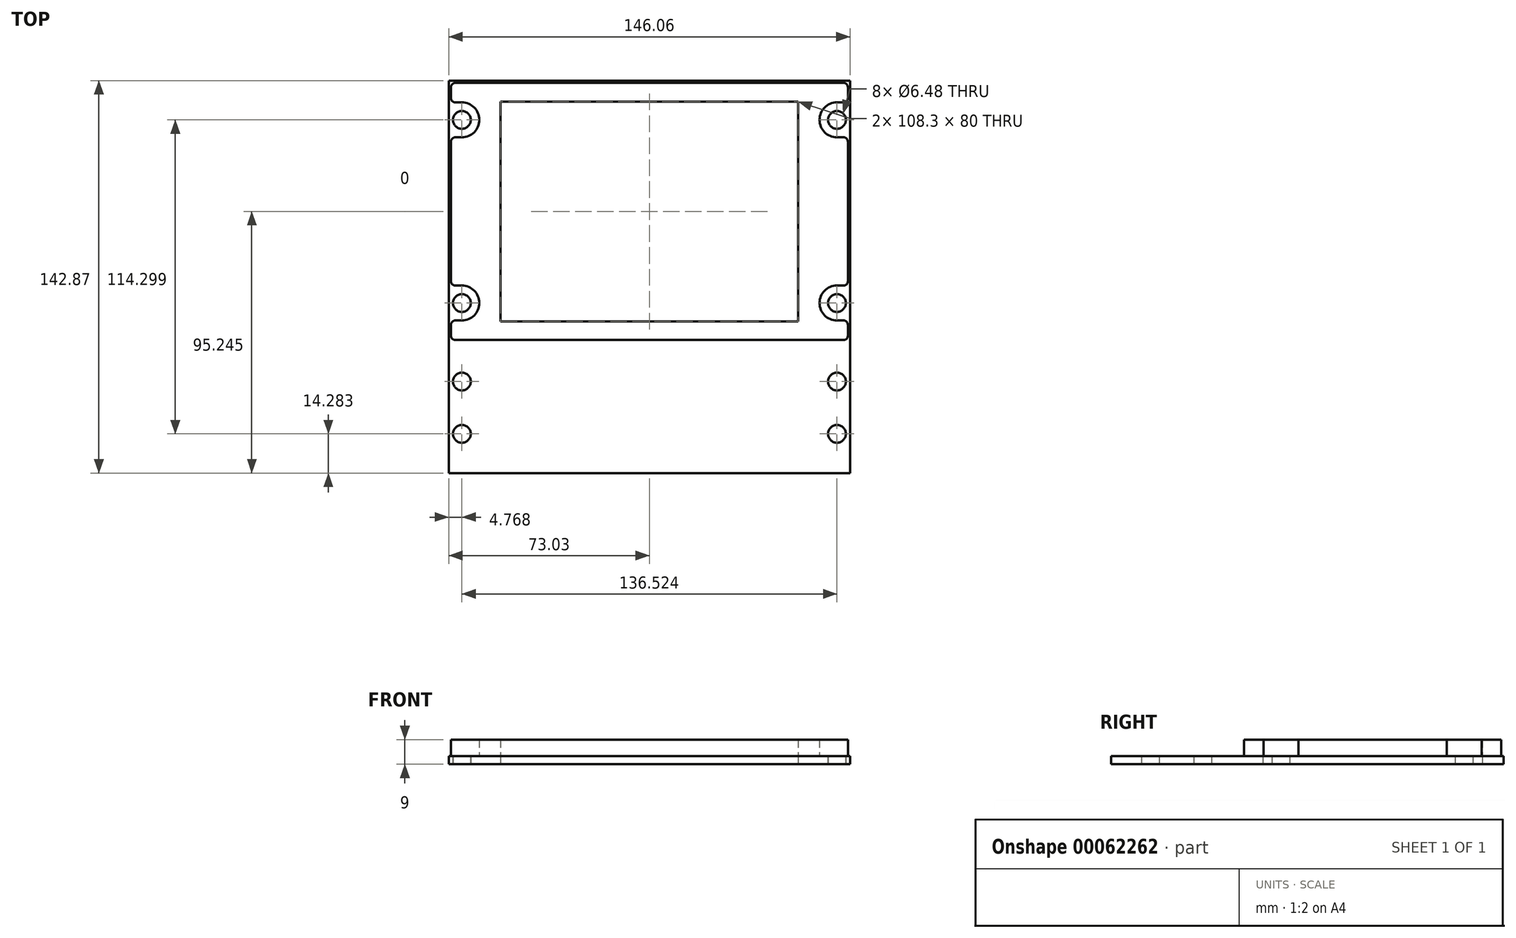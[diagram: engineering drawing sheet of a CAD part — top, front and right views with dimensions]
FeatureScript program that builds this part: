
annotation { "Feature Type Name" : "Feature", "Feature Type Description" : "" }
export const myFeature = defineFeature(function(context is Context, id is Id, definition is map)
    precondition{}
    {
        {
            var Q0;
            Q0=qCreatedBy(makeId("Top.planeOp"),FACE);
            var sketch = newSketch(context, id + "F0", { "sketchPlane" : qUnion([Q0])});
            skLineSegment(sketch, "E0.bottom", {"start": v(-73.03, 57.15) * mm, "end": v(73.03, 57.15) * mm});
            skLineSegment(sketch, "E0.top", {"start": v(-73.03, -38.1) * mm, "end": v(73.03, -38.1) * mm});
            skLineSegment(sketch, "E0.left", {"start": v(-73.03, 57.15) * mm, "end": v(-73.02, -38.1) * mm});
            skLineSegment(sketch, "E0.right", {"start": v(73.03, 57.15) * mm, "end": v(73.03, -38.1) * mm});
            skCircle(sketch, "E1", {"center": v(-68.26, 42.86) * mm, "radius": 3.24 * mm});
            skLineSegment(sketch, "E2", {"start": v(-73.03, 9.52) * mm, "end": v(-67.9, 9.52) * mm});
            skLineSegment(sketch, "E3.MirrorCS", {"start": v(73.03, 57.15) * mm, "end": v(73.02, -38.1) * mm});
            skCircle(sketch, "E4.MirrorC", {"center": v(68.26, 42.86) * mm, "radius": 3.24 * mm});
            skLineSegment(sketch, "E5.bottom", {"start": v(-72.23, 56.35) * mm, "end": v(72.23, 56.35) * mm});
            skLineSegment(sketch, "E5.top", {"start": v(-72.23, -37.3) * mm, "end": v(72.23, -37.3) * mm});
            skLineSegment(sketch, "E5.left", {"start": v(-72.22, 56.35) * mm, "end": v(-72.22, 49.21) * mm});
            skLineSegment(sketch, "E5.right", {"start": v(72.22, 56.35) * mm, "end": v(72.22, 49.21) * mm});
            skPoint(sketch, "E5.middle", {"position": v(0, 9.52) * mm});
            skPoint(sketch, "E5.middle.positionSnap0", {"position": v(0, 57.15) * mm});
            skPoint(sketch, "E5.centerSnap0", {"position": v(0, 57.15) * mm});
            skLineSegment(sketch, "E6.trimOffspring", {"start": v(-72.22, 36.51) * mm, "end": v(-72.22, -17.46) * mm});
            skCircle(sketch, "E7.MirrorC", {"center": v(-68.26, -23.81) * mm, "radius": 3.24 * mm});
            skLineSegment(sketch, "E8.trimOffspring", {"start": v(-72.22, -30.16) * mm, "end": v(-72.22, -37.3) * mm});
            skLineSegment(sketch, "E9", {"start": v(0, 59.28) * mm, "end": v(0, 57.15) * mm});
            skLineSegment(sketch, "E10.trimOffspring", {"start": v(72.22, 36.51) * mm, "end": v(72.22, -17.46) * mm});
            skLineSegment(sketch, "E11.trimOffspring", {"start": v(72.22, -30.16) * mm, "end": v(72.22, -37.3) * mm});
            skCircle(sketch, "E12.MirrorC", {"center": v(68.26, -23.81) * mm, "radius": 3.24 * mm});
            skLineSegment(sketch, "E13", {"start": v(-68.26, 49.21) * mm, "end": v(-72.22, 49.21) * mm});
            skLineSegment(sketch, "E14", {"start": v(-68.26, 36.51) * mm, "end": v(-72.22, 36.51) * mm});
            skArc(sketch, "E15.trimOffspring", {"start": v(-68.26, 36.51) * mm, "mid": v(-61.91, 42.86) * mm, "end": v(-68.26, 49.21) * mm});
            skLineSegment(sketch, "E16.MirrorCS", {"start": v(68.26, 49.21) * mm, "end": v(72.22, 49.21) * mm});
            skArc(sketch, "E17.MirrorCS", {"start": v(68.26, 36.51) * mm, "mid": v(61.91, 42.86) * mm, "end": v(68.26, 49.21) * mm});
            skLineSegment(sketch, "E18.MirrorCS", {"start": v(68.26, 36.51) * mm, "end": v(72.22, 36.51) * mm});
            skLineSegment(sketch, "E19.MirrorCS", {"start": v(-68.26, -30.16) * mm, "end": v(-72.22, -30.16) * mm});
            skArc(sketch, "E20.MirrorCS", {"start": v(-68.26, -17.46) * mm, "mid": v(-61.91, -23.81) * mm, "end": v(-68.26, -30.16) * mm});
            skLineSegment(sketch, "E21.MirrorCS", {"start": v(-68.26, -17.46) * mm, "end": v(-72.22, -17.46) * mm});
            skLineSegment(sketch, "E22.MirrorCS", {"start": v(68.26, -30.16) * mm, "end": v(72.23, -30.16) * mm});
            skArc(sketch, "E23.MirrorCS", {"start": v(68.26, -17.46) * mm, "mid": v(61.91, -23.81) * mm, "end": v(68.26, -30.16) * mm});
            skLineSegment(sketch, "E24.MirrorCS", {"start": v(68.26, -17.46) * mm, "end": v(72.23, -17.46) * mm});
            skSolve(sketch);
        }
        {
            var Q0;
            {var subQ3=sQuery(id+"F0.wireOp",EDGE,"E0.bottom");Q0=makeQuery(id+"F0.imprint","IMPRINT",FACE,{"disambiguationData":[TD([[makeQuery(id+"F0.imprint","IMPRINT",EDGE,{"derivedFrom":subQ3}),-1.0]])]});}
            var Q1;
            Q1=makeQuery(id+"F0.imprint","IMPRINT",FACE,{"disambiguationData":[TD([[makeQuery(id+"F0.imprint","IMPRINT",EDGE,{"derivedFrom":sQuery(id+"F0.wireOp",EDGE,"0KsHYRzl-QeBp-Sicu-B30s-vmT9e8yUwkHf")}),-1.0]])]});
            var Q2;
            {var subQ5=sQuery(id+"F0.wireOp",EDGE,"E0.top");Q2=makeQuery(id+"F0.imprint","IMPRINT",FACE,{"disambiguationData":[TD([[makeQuery(id+"F0.imprint","IMPRINT",EDGE,{"derivedFrom":subQ5}),1.0]])]});}
            var Q3;
            Q3=makeQuery(id+"F0.imprint","IMPRINT",FACE,{"disambiguationData":[TD([[makeQuery(id+"F0.imprint","IMPRINT",EDGE,{"derivedFrom":sQuery(id+"F0.wireOp",EDGE,"E5.bottom")}),-1.0]])]});
            extrude(context, id + "F1", {"entities" : qUnion([Q0, Q1, Q2, Q3]), "oppositeDirection" : true, "depth" : 3 * mm, "offsetDistance" : 25 * mm});
        }
        {
            var Q0;
            Q0=makeQuery(id+"F0.imprint","IMPRINT",FACE,{"disambiguationData":[TD([[makeQuery(id+"F0.imprint","IMPRINT",EDGE,{"derivedFrom":sQuery(id+"F0.wireOp",EDGE,"E5.bottom")}),-1.0]])]});
            extrude(context, id + "F2", {"entities" : qUnion([Q0]), "depth" : 6 * mm, "offsetDistance" : 25 * mm});
        }
        {
            var Q0;
            Q0=makeQuery(id+"F2.opExtrude","SWEPT_EDGE",EDGE,{"disambiguationData":[OSD([sQuery(id+"F0.wireOp",EDGE,"E5.bottom"),sQuery(id+"F0.wireOp",EDGE,"E5.left")])]});
            var Q1;
            Q1=makeQuery(id+"F2.opExtrude","SWEPT_EDGE",EDGE,{"disambiguationData":[OSD([sQuery(id+"F0.wireOp",EDGE,"E5.left"),sQuery(id+"F0.wireOp",EDGE,"KYFBzgIQ-4Zqs-6R5z-qhiH-rvfPci5RRXDs")])]});
            var Q2;
            Q2=makeQuery(id+"F2.opExtrude","SWEPT_EDGE",EDGE,{"disambiguationData":[OSD([sQuery(id+"F0.wireOp",EDGE,"y0Ednotj-fgLE-47Of-3iWq-vnumbfe9Me7E"),sQuery(id+"F0.wireOp",EDGE,"E6.trimOffspring")])]});
            var Q3;
            Q3=makeQuery(id+"F2.opExtrude","SWEPT_EDGE",EDGE,{"disambiguationData":[OSD([sQuery(id+"F0.wireOp",EDGE,"E6.trimOffspring"),sQuery(id+"F0.wireOp",EDGE,"553364b0-0c50-41da-a4d1-f82c899684470.MirrorCS")])]});
            var Q4;
            Q4=makeQuery(id+"F2.opExtrude","SWEPT_EDGE",EDGE,{"disambiguationData":[OSD([sQuery(id+"F0.wireOp",EDGE,"2d0b2af7-1972-4472-80e1-425fef26b84a0.MirrorCS"),sQuery(id+"F0.wireOp",EDGE,"E8.trimOffspring")])]});
            var Q5;
            Q5=makeQuery(id+"F2.opExtrude","SWEPT_EDGE",EDGE,{"disambiguationData":[OSD([sQuery(id+"F0.wireOp",EDGE,"E5.top"),sQuery(id+"F0.wireOp",EDGE,"E8.trimOffspring")])]});
            var Q6;
            Q6=makeQuery(id+"F2.opExtrude","SWEPT_EDGE",EDGE,{"disambiguationData":[OSD([sQuery(id+"F0.wireOp",EDGE,"E5.top"),sQuery(id+"F0.wireOp",EDGE,"E11.trimOffspring")])]});
            var Q7;
            Q7=makeQuery(id+"F2.opExtrude","SWEPT_EDGE",EDGE,{"disambiguationData":[OSD([sQuery(id+"F0.wireOp",EDGE,"6b0da2aa-3882-46fa-a501-ba939454f24d0.MirrorCS"),sQuery(id+"F0.wireOp",EDGE,"E11.trimOffspring")])]});
            var Q8;
            Q8=makeQuery(id+"F2.opExtrude","SWEPT_EDGE",EDGE,{"disambiguationData":[OSD([sQuery(id+"F0.wireOp",EDGE,"23beaa88-9077-45f1-bc4f-ba4309250fa40.MirrorCS"),sQuery(id+"F0.wireOp",EDGE,"E10.trimOffspring")])]});
            var Q9;
            Q9=makeQuery(id+"F2.opExtrude","SWEPT_EDGE",EDGE,{"disambiguationData":[OSD([sQuery(id+"F0.wireOp",EDGE,"E5.right"),sQuery(id+"F0.wireOp",EDGE,"76e7f314-1e51-4c87-a9a9-bf629407e17e0.MirrorCS")])]});
            var Q10;
            Q10=makeQuery(id+"F2.opExtrude","SWEPT_EDGE",EDGE,{"disambiguationData":[OSD([sQuery(id+"F0.wireOp",EDGE,"E5.bottom"),sQuery(id+"F0.wireOp",EDGE,"E5.right")])]});
            var Q11;
            Q11=makeQuery(id+"F2.opExtrude","SWEPT_EDGE",EDGE,{"disambiguationData":[OSD([sQuery(id+"F0.wireOp",EDGE,"fdf2bb90-056c-49c9-a4f4-28e15fb56c020.MirrorCS"),sQuery(id+"F0.wireOp",EDGE,"E10.trimOffspring")])]});
            fillet(context, id + "F3", {"entities" : qUnion([Q0, Q1, Q2, Q3, Q4, Q5, Q6, Q7, Q8, Q9, Q10, Q11]), "radius" : 1.59 * mm, "tangentPropagation" : true, "allowEdgeOverflow" : false});
        }
        {
            var Q0;
            Q0=makeQuery(id+"F2.opExtrude","CAP_FACE",FACE,{"disambiguationData":[OSD([sQuery(id+"F0.wireOp",EDGE,"0KsHYRzl-QeBp-Sicu-B30s-vmT9e8yUwkHf"),sQuery(id+"F0.wireOp",EDGE,"E5.bottom"),sQuery(id+"F0.wireOp",EDGE,"E5.top"),sQuery(id+"F0.wireOp",EDGE,"E5.left"),sQuery(id+"F0.wireOp",EDGE,"E5.right"),sQuery(id+"F0.wireOp",EDGE,"KYFBzgIQ-4Zqs-6R5z-qhiH-rvfPci5RRXDs"),sQuery(id+"F0.wireOp",EDGE,"y0Ednotj-fgLE-47Of-3iWq-vnumbfe9Me7E"),sQuery(id+"F0.wireOp",EDGE,"E6.trimOffspring"),sQuery(id+"F0.wireOp",EDGE,"2a2d7b29-b02f-4e17-9193-bcc7f10cbe761.MirrorCS"),sQuery(id+"F0.wireOp",EDGE,"2d0b2af7-1972-4472-80e1-425fef26b84a0.MirrorCS"),sQuery(id+"F0.wireOp",EDGE,"553364b0-0c50-41da-a4d1-f82c899684470.MirrorCS"),sQuery(id+"F0.wireOp",EDGE,"E8.trimOffspring"),sQuery(id+"F0.wireOp",EDGE,"76e7f314-1e51-4c87-a9a9-bf629407e17e0.MirrorCS"),sQuery(id+"F0.wireOp",EDGE,"802900b7-2ba9-4d70-825f-09b2bce8e5960.MirrorCS"),sQuery(id+"F0.wireOp",EDGE,"fdf2bb90-056c-49c9-a4f4-28e15fb56c020.MirrorCS"),sQuery(id+"F0.wireOp",EDGE,"23beaa88-9077-45f1-bc4f-ba4309250fa40.MirrorCS"),sQuery(id+"F0.wireOp",EDGE,"49d2e7f7-8f5b-4fc1-bffe-4eb2e1ab077b0.MirrorCS"),sQuery(id+"F0.wireOp",EDGE,"6b0da2aa-3882-46fa-a501-ba939454f24d0.MirrorCS"),sQuery(id+"F0.wireOp",EDGE,"E10.trimOffspring"),sQuery(id+"F0.wireOp",EDGE,"E11.trimOffspring")])],"isStart":false});
            var sketch = newSketch(context, id + "F4", { "sketchPlane" : qUnion([Q0])});
            skLineSegment(sketch, "E25", {"start": v(0, 56.35) * mm, "end": v(0, 54.26) * mm});
            skLineSegment(sketch, "E26.bottom", {"start": v(-2, 49.52) * mm, "end": v(-26, 49.52) * mm});
            skLineSegment(sketch, "E26.top", {"start": v(-2, 41.52) * mm, "end": v(-26, 41.52) * mm});
            skLineSegment(sketch, "E26.left", {"start": v(-2, 49.52) * mm, "end": v(-2, 41.52) * mm});
            skLineSegment(sketch, "E26.right", {"start": v(-26, 49.52) * mm, "end": v(-26, 41.52) * mm});
            skLineSegment(sketch, "E27.bottom", {"start": v(-30, 49.52) * mm, "end": v(-54.15, 49.52) * mm});
            skLineSegment(sketch, "E27.top", {"start": v(-30, 41.52) * mm, "end": v(-54.15, 41.52) * mm});
            skLineSegment(sketch, "E27.left", {"start": v(-30, 49.52) * mm, "end": v(-30, 41.52) * mm});
            skLineSegment(sketch, "E27.right", {"start": v(-54.15, 49.52) * mm, "end": v(-54.15, 41.52) * mm});
            skLineSegment(sketch, "E28.MirrorCS", {"start": v(30, 41.52) * mm, "end": v(54.15, 41.52) * mm});
            skLineSegment(sketch, "E29.MirrorCS", {"start": v(2, 41.52) * mm, "end": v(26, 41.52) * mm});
            skLineSegment(sketch, "E30.MirrorCS", {"start": v(30, 49.52) * mm, "end": v(54.15, 49.52) * mm});
            skLineSegment(sketch, "E31.MirrorCS", {"start": v(2, 49.52) * mm, "end": v(2, 41.52) * mm});
            skLineSegment(sketch, "E32.MirrorCS", {"start": v(30, 49.52) * mm, "end": v(30, 41.52) * mm});
            skLineSegment(sketch, "E33.MirrorCS", {"start": v(2, 49.52) * mm, "end": v(26, 49.52) * mm});
            skLineSegment(sketch, "E34.MirrorCS", {"start": v(26, 49.52) * mm, "end": v(26, 41.52) * mm});
            skLineSegment(sketch, "E35.MirrorCS", {"start": v(54.15, 49.52) * mm, "end": v(54.15, 41.52) * mm});
            skLineSegment(sketch, "E36.0.1.0", {"start": v(-2, 37.52) * mm, "end": v(-26, 37.52) * mm});
            skLineSegment(sketch, "E36.0.1.1", {"start": v(-30, 29.52) * mm, "end": v(-54.15, 29.52) * mm});
            skLineSegment(sketch, "E36.0.1.2", {"start": v(26, 37.52) * mm, "end": v(26, 29.52) * mm});
            skLineSegment(sketch, "E36.0.1.3", {"start": v(30, 37.52) * mm, "end": v(54.15, 37.52) * mm});
            skLineSegment(sketch, "E36.0.1.4", {"start": v(-26, 37.52) * mm, "end": v(-26, 29.52) * mm});
            skLineSegment(sketch, "E36.0.1.5", {"start": v(30, 29.52) * mm, "end": v(54.15, 29.52) * mm});
            skLineSegment(sketch, "E36.0.1.6", {"start": v(2, 37.52) * mm, "end": v(2, 29.52) * mm});
            skLineSegment(sketch, "E36.0.1.7", {"start": v(30, 37.52) * mm, "end": v(30, 29.52) * mm});
            skLineSegment(sketch, "E36.0.1.8", {"start": v(-54.15, 37.52) * mm, "end": v(-54.15, 29.52) * mm});
            skLineSegment(sketch, "E36.0.1.9", {"start": v(54.15, 37.53) * mm, "end": v(54.15, 29.52) * mm});
            skLineSegment(sketch, "E36.0.1.10", {"start": v(-2, 37.52) * mm, "end": v(-2, 29.52) * mm});
            skLineSegment(sketch, "E36.0.1.11", {"start": v(2, 29.52) * mm, "end": v(26, 29.52) * mm});
            skLineSegment(sketch, "E36.0.1.12", {"start": v(2, 37.52) * mm, "end": v(26, 37.52) * mm});
            skLineSegment(sketch, "E36.0.1.13", {"start": v(-30, 37.52) * mm, "end": v(-30, 29.52) * mm});
            skLineSegment(sketch, "E36.0.1.14", {"start": v(-30, 37.52) * mm, "end": v(-54.15, 37.52) * mm});
            skLineSegment(sketch, "E36.0.1.15", {"start": v(-2, 29.52) * mm, "end": v(-26, 29.52) * mm});
            skLineSegment(sketch, "E36.0.2.0", {"start": v(-2, 25.52) * mm, "end": v(-26, 25.52) * mm});
            skLineSegment(sketch, "E36.0.2.1", {"start": v(-30, 17.52) * mm, "end": v(-54.15, 17.52) * mm});
            skLineSegment(sketch, "E36.0.2.2", {"start": v(26, 25.52) * mm, "end": v(26, 17.52) * mm});
            skLineSegment(sketch, "E36.0.2.3", {"start": v(30, 25.52) * mm, "end": v(54.15, 25.52) * mm});
            skLineSegment(sketch, "E36.0.2.4", {"start": v(-26, 25.52) * mm, "end": v(-26, 17.52) * mm});
            skLineSegment(sketch, "E36.0.2.5", {"start": v(30, 17.52) * mm, "end": v(54.15, 17.52) * mm});
            skLineSegment(sketch, "E36.0.2.6", {"start": v(2, 25.52) * mm, "end": v(2, 17.52) * mm});
            skLineSegment(sketch, "E36.0.2.7", {"start": v(30, 25.52) * mm, "end": v(30, 17.52) * mm});
            skLineSegment(sketch, "E36.0.2.8", {"start": v(-54.15, 25.52) * mm, "end": v(-54.15, 17.52) * mm});
            skLineSegment(sketch, "E36.0.2.9", {"start": v(54.15, 25.53) * mm, "end": v(54.15, 17.52) * mm});
            skLineSegment(sketch, "E36.0.2.10", {"start": v(-2, 25.52) * mm, "end": v(-2, 17.52) * mm});
            skLineSegment(sketch, "E36.0.2.11", {"start": v(2, 17.52) * mm, "end": v(26, 17.52) * mm});
            skLineSegment(sketch, "E36.0.2.12", {"start": v(2, 25.52) * mm, "end": v(26, 25.52) * mm});
            skLineSegment(sketch, "E36.0.2.13", {"start": v(-30, 25.52) * mm, "end": v(-30, 17.52) * mm});
            skLineSegment(sketch, "E36.0.2.14", {"start": v(-30, 25.52) * mm, "end": v(-54.15, 25.52) * mm});
            skLineSegment(sketch, "E36.0.2.15", {"start": v(-2, 17.52) * mm, "end": v(-26, 17.52) * mm});
            skLineSegment(sketch, "E36.0.3.0", {"start": v(-2, 13.52) * mm, "end": v(-26, 13.52) * mm});
            skLineSegment(sketch, "E36.0.3.1", {"start": v(-30, 5.52) * mm, "end": v(-54.15, 5.52) * mm});
            skLineSegment(sketch, "E36.0.3.2", {"start": v(26, 13.53) * mm, "end": v(26, 5.53) * mm});
            skLineSegment(sketch, "E36.0.3.3", {"start": v(30, 13.52) * mm, "end": v(54.15, 13.52) * mm});
            skLineSegment(sketch, "E36.0.3.4", {"start": v(-26, 13.52) * mm, "end": v(-26, 5.52) * mm});
            skLineSegment(sketch, "E36.0.3.5", {"start": v(30, 5.52) * mm, "end": v(54.15, 5.52) * mm});
            skLineSegment(sketch, "E36.0.3.6", {"start": v(2, 13.52) * mm, "end": v(2, 5.52) * mm});
            skLineSegment(sketch, "E36.0.3.7", {"start": v(30, 13.53) * mm, "end": v(30, 5.53) * mm});
            skLineSegment(sketch, "E36.0.3.8", {"start": v(-54.15, 13.52) * mm, "end": v(-54.15, 5.52) * mm});
            skLineSegment(sketch, "E36.0.3.9", {"start": v(54.15, 13.53) * mm, "end": v(54.15, 5.52) * mm});
            skLineSegment(sketch, "E36.0.3.10", {"start": v(-2, 13.52) * mm, "end": v(-2, 5.52) * mm});
            skLineSegment(sketch, "E36.0.3.11", {"start": v(2, 5.52) * mm, "end": v(26, 5.52) * mm});
            skLineSegment(sketch, "E36.0.3.12", {"start": v(2, 13.52) * mm, "end": v(26, 13.52) * mm});
            skLineSegment(sketch, "E36.0.3.13", {"start": v(-30, 13.52) * mm, "end": v(-30, 5.52) * mm});
            skLineSegment(sketch, "E36.0.3.14", {"start": v(-30, 13.52) * mm, "end": v(-54.15, 13.52) * mm});
            skLineSegment(sketch, "E36.0.3.15", {"start": v(-2, 5.52) * mm, "end": v(-26, 5.52) * mm});
            skLineSegment(sketch, "E36.0.4.0", {"start": v(-2, 1.52) * mm, "end": v(-26, 1.52) * mm});
            skLineSegment(sketch, "E36.0.4.1", {"start": v(-30, -6.48) * mm, "end": v(-54.15, -6.48) * mm});
            skLineSegment(sketch, "E36.0.4.2", {"start": v(26, 1.53) * mm, "end": v(26, -6.47) * mm});
            skLineSegment(sketch, "E36.0.4.3", {"start": v(30, 1.52) * mm, "end": v(54.15, 1.53) * mm});
            skLineSegment(sketch, "E36.0.4.4", {"start": v(-26, 1.52) * mm, "end": v(-26, -6.48) * mm});
            skLineSegment(sketch, "E36.0.4.5", {"start": v(30, -6.48) * mm, "end": v(54.15, -6.47) * mm});
            skLineSegment(sketch, "E36.0.4.6", {"start": v(2, 1.52) * mm, "end": v(2, -6.48) * mm});
            skLineSegment(sketch, "E36.0.4.7", {"start": v(30, 1.53) * mm, "end": v(30, -6.47) * mm});
            skLineSegment(sketch, "E36.0.4.8", {"start": v(-54.15, 1.52) * mm, "end": v(-54.15, -6.48) * mm});
            skLineSegment(sketch, "E36.0.4.9", {"start": v(54.15, 1.53) * mm, "end": v(54.15, -6.48) * mm});
            skLineSegment(sketch, "E36.0.4.10", {"start": v(-2, 1.52) * mm, "end": v(-2, -6.48) * mm});
            skLineSegment(sketch, "E36.0.4.11", {"start": v(2, -6.48) * mm, "end": v(26, -6.47) * mm});
            skLineSegment(sketch, "E36.0.4.12", {"start": v(2, 1.52) * mm, "end": v(26, 1.53) * mm});
            skLineSegment(sketch, "E36.0.4.13", {"start": v(-30, 1.52) * mm, "end": v(-30, -6.48) * mm});
            skLineSegment(sketch, "E36.0.4.14", {"start": v(-30, 1.52) * mm, "end": v(-54.15, 1.52) * mm});
            skLineSegment(sketch, "E36.0.4.15", {"start": v(-2, -6.48) * mm, "end": v(-26, -6.48) * mm});
            skLineSegment(sketch, "E36.0.5.0", {"start": v(-2, -10.47) * mm, "end": v(-26, -10.47) * mm});
            skLineSegment(sketch, "E36.0.5.1", {"start": v(-30, -18.47) * mm, "end": v(-54.15, -18.47) * mm});
            skLineSegment(sketch, "E36.0.5.2", {"start": v(26, -10.47) * mm, "end": v(26, -18.47) * mm});
            skLineSegment(sketch, "E36.0.5.3", {"start": v(30, -10.47) * mm, "end": v(54.15, -10.47) * mm});
            skLineSegment(sketch, "E36.0.5.4", {"start": v(-26, -10.47) * mm, "end": v(-26, -18.47) * mm});
            skLineSegment(sketch, "E36.0.5.5", {"start": v(30, -18.47) * mm, "end": v(54.15, -18.47) * mm});
            skLineSegment(sketch, "E36.0.5.6", {"start": v(2, -10.47) * mm, "end": v(2, -18.47) * mm});
            skLineSegment(sketch, "E36.0.5.7", {"start": v(30, -10.47) * mm, "end": v(30, -18.47) * mm});
            skLineSegment(sketch, "E36.0.5.8", {"start": v(-54.15, -10.47) * mm, "end": v(-54.15, -18.47) * mm});
            skLineSegment(sketch, "E36.0.5.9", {"start": v(54.15, -10.47) * mm, "end": v(54.15, -18.47) * mm});
            skLineSegment(sketch, "E36.0.5.10", {"start": v(-2, -10.47) * mm, "end": v(-2, -18.47) * mm});
            skLineSegment(sketch, "E36.0.5.11", {"start": v(2, -18.47) * mm, "end": v(26, -18.47) * mm});
            skLineSegment(sketch, "E36.0.5.12", {"start": v(2, -10.47) * mm, "end": v(26, -10.47) * mm});
            skLineSegment(sketch, "E36.0.5.13", {"start": v(-30, -10.47) * mm, "end": v(-30, -18.47) * mm});
            skLineSegment(sketch, "E36.0.5.14", {"start": v(-30, -10.47) * mm, "end": v(-54.15, -10.47) * mm});
            skLineSegment(sketch, "E36.0.5.15", {"start": v(-2, -18.47) * mm, "end": v(-26, -18.47) * mm});
            skLineSegment(sketch, "E36.0.6.0", {"start": v(-2, -22.47) * mm, "end": v(-26, -22.47) * mm});
            skLineSegment(sketch, "E36.0.6.1", {"start": v(-30, -30.47) * mm, "end": v(-54.15, -30.47) * mm});
            skLineSegment(sketch, "E36.0.6.2", {"start": v(26, -22.47) * mm, "end": v(26, -30.47) * mm});
            skLineSegment(sketch, "E36.0.6.3", {"start": v(30, -22.47) * mm, "end": v(54.15, -22.47) * mm});
            skLineSegment(sketch, "E36.0.6.4", {"start": v(-26, -22.47) * mm, "end": v(-26, -30.47) * mm});
            skLineSegment(sketch, "E36.0.6.5", {"start": v(30, -30.47) * mm, "end": v(54.15, -30.47) * mm});
            skLineSegment(sketch, "E36.0.6.6", {"start": v(2, -22.47) * mm, "end": v(2, -30.47) * mm});
            skLineSegment(sketch, "E36.0.6.7", {"start": v(30, -22.47) * mm, "end": v(30, -30.47) * mm});
            skLineSegment(sketch, "E36.0.6.8", {"start": v(-54.15, -22.47) * mm, "end": v(-54.15, -30.47) * mm});
            skLineSegment(sketch, "E36.0.6.9", {"start": v(54.15, -22.47) * mm, "end": v(54.15, -30.47) * mm});
            skLineSegment(sketch, "E36.0.6.10", {"start": v(-2, -22.47) * mm, "end": v(-2, -30.47) * mm});
            skLineSegment(sketch, "E36.0.6.11", {"start": v(2, -30.47) * mm, "end": v(26, -30.47) * mm});
            skLineSegment(sketch, "E36.0.6.12", {"start": v(2, -22.47) * mm, "end": v(26, -22.47) * mm});
            skLineSegment(sketch, "E36.0.6.13", {"start": v(-30, -22.47) * mm, "end": v(-30, -30.47) * mm});
            skLineSegment(sketch, "E36.0.6.14", {"start": v(-30, -22.47) * mm, "end": v(-54.15, -22.47) * mm});
            skLineSegment(sketch, "E36.0.6.15", {"start": v(-2, -30.47) * mm, "end": v(-26, -30.47) * mm});
            skLineSegment(sketch, "E36.direction1", {"start": v(-54.15, 41.52) * mm, "end": v(-29.15, 41.52) * mm, "construction": true});
            skLineSegment(sketch, "E36.direction2", {"start": v(-54.15, 41.52) * mm, "end": v(-54.15, 29.52) * mm, "construction": true});
            skLineSegment(sketch, "E37", {"start": v(-2, 9.52) * mm, "end": v(-6.78, 9.52) * mm});
            skSolve(sketch);
        }
        {
            var Q0;
            Q0 = qSketchRegion(id + "F4", true);
            extrude(context, id + "F5", {"entities" : qUnion([Q0]), "operationType" : NewBodyOperationType.REMOVE, "oppositeDirection" : true, "depth" : 25 * mm, "offsetDistance" : 25 * mm});
        }
        {
            var Q0;
            Q0=makeQuery(id+"F5.boolean.opBoolean","COPY",EDGE,{"derivedFrom":makeQuery(id+"F5.opExtrude","SWEPT_EDGE",EDGE,{"disambiguationData":[OSD([sQuery(id+"F4.wireOp",EDGE,"E27.bottom"),sQuery(id+"F4.wireOp",EDGE,"E27.right")])]})});
            var Q1;
            Q1=makeQuery(id+"F5.boolean.opBoolean","COPY",EDGE,{"derivedFrom":makeQuery(id+"F5.opExtrude","SWEPT_EDGE",EDGE,{"disambiguationData":[OSD([sQuery(id+"F4.wireOp",EDGE,"E27.top"),sQuery(id+"F4.wireOp",EDGE,"E27.right")])]})});
            var Q2;
            Q2=makeQuery(id+"F5.boolean.opBoolean","COPY",EDGE,{"derivedFrom":makeQuery(id+"F5.opExtrude","SWEPT_EDGE",EDGE,{"disambiguationData":[OSD([sQuery(id+"F4.wireOp",EDGE,"E27.top"),sQuery(id+"F4.wireOp",EDGE,"E27.left")])]})});
            var Q3;
            Q3=makeQuery(id+"F5.boolean.opBoolean","COPY",EDGE,{"derivedFrom":makeQuery(id+"F5.opExtrude","SWEPT_EDGE",EDGE,{"disambiguationData":[OSD([sQuery(id+"F4.wireOp",EDGE,"E27.bottom"),sQuery(id+"F4.wireOp",EDGE,"E27.left")])]})});
            var Q4;
            Q4=makeQuery(id+"F5.boolean.opBoolean","COPY",EDGE,{"derivedFrom":makeQuery(id+"F5.opExtrude","SWEPT_EDGE",EDGE,{"disambiguationData":[OSD([sQuery(id+"F4.wireOp",EDGE,"E36.0.1.13"),sQuery(id+"F4.wireOp",EDGE,"E36.0.1.14")])]})});
            var Q5;
            Q5=makeQuery(id+"F5.boolean.opBoolean","COPY",EDGE,{"derivedFrom":makeQuery(id+"F5.opExtrude","SWEPT_EDGE",EDGE,{"disambiguationData":[OSD([sQuery(id+"F4.wireOp",EDGE,"E36.0.2.13"),sQuery(id+"F4.wireOp",EDGE,"E36.0.2.14")])]})});
            var Q6;
            Q6=makeQuery(id+"F5.boolean.opBoolean","COPY",EDGE,{"derivedFrom":makeQuery(id+"F5.opExtrude","SWEPT_EDGE",EDGE,{"disambiguationData":[OSD([sQuery(id+"F4.wireOp",EDGE,"E36.0.3.13"),sQuery(id+"F4.wireOp",EDGE,"E36.0.3.14")])]})});
            var Q7;
            Q7=makeQuery(id+"F5.boolean.opBoolean","COPY",EDGE,{"derivedFrom":makeQuery(id+"F5.opExtrude","SWEPT_EDGE",EDGE,{"disambiguationData":[OSD([sQuery(id+"F4.wireOp",EDGE,"E36.0.4.13"),sQuery(id+"F4.wireOp",EDGE,"E36.0.4.14")])]})});
            var Q8;
            Q8=makeQuery(id+"F5.boolean.opBoolean","COPY",EDGE,{"derivedFrom":makeQuery(id+"F5.opExtrude","SWEPT_EDGE",EDGE,{"disambiguationData":[OSD([sQuery(id+"F4.wireOp",EDGE,"E36.0.5.13"),sQuery(id+"F4.wireOp",EDGE,"E36.0.5.14")])]})});
            var Q9;
            Q9=makeQuery(id+"F5.boolean.opBoolean","COPY",EDGE,{"derivedFrom":makeQuery(id+"F5.opExtrude","SWEPT_EDGE",EDGE,{"disambiguationData":[OSD([sQuery(id+"F4.wireOp",EDGE,"E36.0.6.13"),sQuery(id+"F4.wireOp",EDGE,"E36.0.6.14")])]})});
            var Q10;
            Q10=makeQuery(id+"F5.boolean.opBoolean","COPY",EDGE,{"derivedFrom":makeQuery(id+"F5.opExtrude","SWEPT_EDGE",EDGE,{"disambiguationData":[OSD([sQuery(id+"F4.wireOp",EDGE,"E36.0.6.0"),sQuery(id+"F4.wireOp",EDGE,"E36.0.6.10")])]})});
            var Q11;
            Q11=makeQuery(id+"F5.boolean.opBoolean","COPY",EDGE,{"derivedFrom":makeQuery(id+"F5.opExtrude","SWEPT_EDGE",EDGE,{"disambiguationData":[OSD([sQuery(id+"F4.wireOp",EDGE,"E36.0.5.0"),sQuery(id+"F4.wireOp",EDGE,"E36.0.5.10")])]})});
            var Q12;
            Q12=makeQuery(id+"F5.boolean.opBoolean","COPY",EDGE,{"derivedFrom":makeQuery(id+"F5.opExtrude","SWEPT_EDGE",EDGE,{"disambiguationData":[OSD([sQuery(id+"F4.wireOp",EDGE,"E36.0.4.0"),sQuery(id+"F4.wireOp",EDGE,"E36.0.4.10")])]})});
            var Q13;
            Q13=makeQuery(id+"F5.boolean.opBoolean","COPY",EDGE,{"derivedFrom":makeQuery(id+"F5.opExtrude","SWEPT_EDGE",EDGE,{"disambiguationData":[OSD([sQuery(id+"F4.wireOp",EDGE,"E36.0.3.0"),sQuery(id+"F4.wireOp",EDGE,"E36.0.3.10")])]})});
            var Q14;
            Q14=makeQuery(id+"F5.boolean.opBoolean","COPY",EDGE,{"derivedFrom":makeQuery(id+"F5.opExtrude","SWEPT_EDGE",EDGE,{"disambiguationData":[OSD([sQuery(id+"F4.wireOp",EDGE,"E36.0.2.0"),sQuery(id+"F4.wireOp",EDGE,"E36.0.2.10")])]})});
            var Q15;
            Q15=makeQuery(id+"F5.boolean.opBoolean","COPY",EDGE,{"derivedFrom":makeQuery(id+"F5.opExtrude","SWEPT_EDGE",EDGE,{"disambiguationData":[OSD([sQuery(id+"F4.wireOp",EDGE,"E36.0.1.0"),sQuery(id+"F4.wireOp",EDGE,"E36.0.1.10")])]})});
            var Q16;
            Q16=makeQuery(id+"F5.boolean.opBoolean","COPY",EDGE,{"derivedFrom":makeQuery(id+"F5.opExtrude","SWEPT_EDGE",EDGE,{"disambiguationData":[OSD([sQuery(id+"F4.wireOp",EDGE,"E26.bottom"),sQuery(id+"F4.wireOp",EDGE,"E26.left")])]})});
            var Q17;
            Q17=makeQuery(id+"F5.boolean.opBoolean","COPY",EDGE,{"derivedFrom":makeQuery(id+"F5.opExtrude","SWEPT_EDGE",EDGE,{"disambiguationData":[OSD([sQuery(id+"F4.wireOp",EDGE,"E33.MirrorCS"),sQuery(id+"F4.wireOp",EDGE,"E34.MirrorCS")])]})});
            var Q18;
            Q18=makeQuery(id+"F5.boolean.opBoolean","COPY",EDGE,{"derivedFrom":makeQuery(id+"F5.opExtrude","SWEPT_EDGE",EDGE,{"disambiguationData":[OSD([sQuery(id+"F4.wireOp",EDGE,"E36.0.1.2"),sQuery(id+"F4.wireOp",EDGE,"E36.0.1.12")])]})});
            var Q19;
            Q19=makeQuery(id+"F5.boolean.opBoolean","COPY",EDGE,{"derivedFrom":makeQuery(id+"F5.opExtrude","SWEPT_EDGE",EDGE,{"disambiguationData":[OSD([sQuery(id+"F4.wireOp",EDGE,"E36.0.2.2"),sQuery(id+"F4.wireOp",EDGE,"E36.0.2.12")])]})});
            var Q20;
            Q20=makeQuery(id+"F5.boolean.opBoolean","COPY",EDGE,{"derivedFrom":makeQuery(id+"F5.opExtrude","SWEPT_EDGE",EDGE,{"disambiguationData":[OSD([sQuery(id+"F4.wireOp",EDGE,"E36.0.3.2"),sQuery(id+"F4.wireOp",EDGE,"E36.0.3.12")])]})});
            var Q21;
            Q21=makeQuery(id+"F5.boolean.opBoolean","COPY",EDGE,{"derivedFrom":makeQuery(id+"F5.opExtrude","SWEPT_EDGE",EDGE,{"disambiguationData":[OSD([sQuery(id+"F4.wireOp",EDGE,"E36.0.4.2"),sQuery(id+"F4.wireOp",EDGE,"E36.0.4.12")])]})});
            var Q22;
            Q22=makeQuery(id+"F5.boolean.opBoolean","COPY",EDGE,{"derivedFrom":makeQuery(id+"F5.opExtrude","SWEPT_EDGE",EDGE,{"disambiguationData":[OSD([sQuery(id+"F4.wireOp",EDGE,"E36.0.5.2"),sQuery(id+"F4.wireOp",EDGE,"E36.0.5.12")])]})});
            var Q23;
            Q23=makeQuery(id+"F5.boolean.opBoolean","COPY",EDGE,{"derivedFrom":makeQuery(id+"F5.opExtrude","SWEPT_EDGE",EDGE,{"disambiguationData":[OSD([sQuery(id+"F4.wireOp",EDGE,"E36.0.6.2"),sQuery(id+"F4.wireOp",EDGE,"E36.0.6.12")])]})});
            var Q24;
            Q24=makeQuery(id+"F5.boolean.opBoolean","COPY",EDGE,{"derivedFrom":makeQuery(id+"F5.opExtrude","SWEPT_EDGE",EDGE,{"disambiguationData":[OSD([sQuery(id+"F4.wireOp",EDGE,"E36.0.6.3"),sQuery(id+"F4.wireOp",EDGE,"E36.0.6.9")])]})});
            var Q25;
            Q25=makeQuery(id+"F5.boolean.opBoolean","COPY",EDGE,{"derivedFrom":makeQuery(id+"F5.opExtrude","SWEPT_EDGE",EDGE,{"disambiguationData":[OSD([sQuery(id+"F4.wireOp",EDGE,"E36.0.5.3"),sQuery(id+"F4.wireOp",EDGE,"E36.0.5.9")])]})});
            var Q26;
            Q26=makeQuery(id+"F5.boolean.opBoolean","COPY",EDGE,{"derivedFrom":makeQuery(id+"F5.opExtrude","SWEPT_EDGE",EDGE,{"disambiguationData":[OSD([sQuery(id+"F4.wireOp",EDGE,"E36.0.4.3"),sQuery(id+"F4.wireOp",EDGE,"E36.0.4.9")])]})});
            var Q27;
            Q27=makeQuery(id+"F5.boolean.opBoolean","COPY",EDGE,{"derivedFrom":makeQuery(id+"F5.opExtrude","SWEPT_EDGE",EDGE,{"disambiguationData":[OSD([sQuery(id+"F4.wireOp",EDGE,"E36.0.3.3"),sQuery(id+"F4.wireOp",EDGE,"E36.0.3.9")])]})});
            var Q28;
            Q28=makeQuery(id+"F5.boolean.opBoolean","COPY",EDGE,{"derivedFrom":makeQuery(id+"F5.opExtrude","SWEPT_EDGE",EDGE,{"disambiguationData":[OSD([sQuery(id+"F4.wireOp",EDGE,"E36.0.2.3"),sQuery(id+"F4.wireOp",EDGE,"E36.0.2.9")])]})});
            var Q29;
            Q29=makeQuery(id+"F5.boolean.opBoolean","COPY",EDGE,{"derivedFrom":makeQuery(id+"F5.opExtrude","SWEPT_EDGE",EDGE,{"disambiguationData":[OSD([sQuery(id+"F4.wireOp",EDGE,"E36.0.1.3"),sQuery(id+"F4.wireOp",EDGE,"E36.0.1.9")])]})});
            var Q30;
            Q30=makeQuery(id+"F5.boolean.opBoolean","COPY",EDGE,{"derivedFrom":makeQuery(id+"F5.opExtrude","SWEPT_EDGE",EDGE,{"disambiguationData":[OSD([sQuery(id+"F4.wireOp",EDGE,"E30.MirrorCS"),sQuery(id+"F4.wireOp",EDGE,"E35.MirrorCS")])]})});
            var Q31;
            Q31=makeQuery(id+"F5.boolean.opBoolean","COPY",EDGE,{"derivedFrom":makeQuery(id+"F5.opExtrude","SWEPT_EDGE",EDGE,{"disambiguationData":[OSD([sQuery(id+"F4.wireOp",EDGE,"E26.top"),sQuery(id+"F4.wireOp",EDGE,"E26.left")])]})});
            var Q32;
            Q32=makeQuery(id+"F5.boolean.opBoolean","COPY",EDGE,{"derivedFrom":makeQuery(id+"F5.opExtrude","SWEPT_EDGE",EDGE,{"disambiguationData":[OSD([sQuery(id+"F4.wireOp",EDGE,"E29.MirrorCS"),sQuery(id+"F4.wireOp",EDGE,"E34.MirrorCS")])]})});
            var Q33;
            Q33=makeQuery(id+"F5.boolean.opBoolean","COPY",EDGE,{"derivedFrom":makeQuery(id+"F5.opExtrude","SWEPT_EDGE",EDGE,{"disambiguationData":[OSD([sQuery(id+"F4.wireOp",EDGE,"E28.MirrorCS"),sQuery(id+"F4.wireOp",EDGE,"E35.MirrorCS")])]})});
            var Q34;
            Q34=makeQuery(id+"F5.boolean.opBoolean","COPY",EDGE,{"derivedFrom":makeQuery(id+"F5.opExtrude","SWEPT_EDGE",EDGE,{"disambiguationData":[OSD([sQuery(id+"F4.wireOp",EDGE,"E36.0.1.1"),sQuery(id+"F4.wireOp",EDGE,"E36.0.1.13")])]})});
            var Q35;
            Q35=makeQuery(id+"F5.boolean.opBoolean","COPY",EDGE,{"derivedFrom":makeQuery(id+"F5.opExtrude","SWEPT_EDGE",EDGE,{"disambiguationData":[OSD([sQuery(id+"F4.wireOp",EDGE,"E36.0.1.10"),sQuery(id+"F4.wireOp",EDGE,"E36.0.1.15")])]})});
            var Q36;
            Q36=makeQuery(id+"F5.boolean.opBoolean","COPY",EDGE,{"derivedFrom":makeQuery(id+"F5.opExtrude","SWEPT_EDGE",EDGE,{"disambiguationData":[OSD([sQuery(id+"F4.wireOp",EDGE,"E36.0.1.2"),sQuery(id+"F4.wireOp",EDGE,"E36.0.1.11")])]})});
            var Q37;
            Q37=makeQuery(id+"F5.boolean.opBoolean","COPY",EDGE,{"derivedFrom":makeQuery(id+"F5.opExtrude","SWEPT_EDGE",EDGE,{"disambiguationData":[OSD([sQuery(id+"F4.wireOp",EDGE,"E36.0.1.5"),sQuery(id+"F4.wireOp",EDGE,"E36.0.1.9")])]})});
            var Q38;
            Q38=makeQuery(id+"F5.boolean.opBoolean","COPY",EDGE,{"derivedFrom":makeQuery(id+"F5.opExtrude","SWEPT_EDGE",EDGE,{"disambiguationData":[OSD([sQuery(id+"F4.wireOp",EDGE,"E36.0.2.5"),sQuery(id+"F4.wireOp",EDGE,"E36.0.2.9")])]})});
            var Q39;
            Q39=makeQuery(id+"F5.boolean.opBoolean","COPY",EDGE,{"derivedFrom":makeQuery(id+"F5.opExtrude","SWEPT_EDGE",EDGE,{"disambiguationData":[OSD([sQuery(id+"F4.wireOp",EDGE,"E36.0.2.2"),sQuery(id+"F4.wireOp",EDGE,"E36.0.2.11")])]})});
            var Q40;
            Q40=makeQuery(id+"F5.boolean.opBoolean","COPY",EDGE,{"derivedFrom":makeQuery(id+"F5.opExtrude","SWEPT_EDGE",EDGE,{"disambiguationData":[OSD([sQuery(id+"F4.wireOp",EDGE,"E36.0.2.10"),sQuery(id+"F4.wireOp",EDGE,"E36.0.2.15")])]})});
            var Q41;
            Q41=makeQuery(id+"F5.boolean.opBoolean","COPY",EDGE,{"derivedFrom":makeQuery(id+"F5.opExtrude","SWEPT_EDGE",EDGE,{"disambiguationData":[OSD([sQuery(id+"F4.wireOp",EDGE,"E36.0.2.1"),sQuery(id+"F4.wireOp",EDGE,"E36.0.2.13")])]})});
            var Q42;
            Q42=makeQuery(id+"F5.boolean.opBoolean","COPY",EDGE,{"derivedFrom":makeQuery(id+"F5.opExtrude","SWEPT_EDGE",EDGE,{"disambiguationData":[OSD([sQuery(id+"F4.wireOp",EDGE,"E36.0.3.1"),sQuery(id+"F4.wireOp",EDGE,"E36.0.3.13")])]})});
            var Q43;
            Q43=makeQuery(id+"F5.boolean.opBoolean","COPY",EDGE,{"derivedFrom":makeQuery(id+"F5.opExtrude","SWEPT_EDGE",EDGE,{"disambiguationData":[OSD([sQuery(id+"F4.wireOp",EDGE,"E36.0.4.1"),sQuery(id+"F4.wireOp",EDGE,"E36.0.4.13")])]})});
            var Q44;
            Q44=makeQuery(id+"F5.boolean.opBoolean","COPY",EDGE,{"derivedFrom":makeQuery(id+"F5.opExtrude","SWEPT_EDGE",EDGE,{"disambiguationData":[OSD([sQuery(id+"F4.wireOp",EDGE,"E36.0.5.1"),sQuery(id+"F4.wireOp",EDGE,"E36.0.5.13")])]})});
            var Q45;
            Q45=makeQuery(id+"F5.boolean.opBoolean","COPY",EDGE,{"derivedFrom":makeQuery(id+"F5.opExtrude","SWEPT_EDGE",EDGE,{"disambiguationData":[OSD([sQuery(id+"F4.wireOp",EDGE,"E36.0.6.1"),sQuery(id+"F4.wireOp",EDGE,"E36.0.6.13")])]})});
            var Q46;
            Q46=makeQuery(id+"F5.boolean.opBoolean","COPY",EDGE,{"derivedFrom":makeQuery(id+"F5.opExtrude","SWEPT_EDGE",EDGE,{"disambiguationData":[OSD([sQuery(id+"F4.wireOp",EDGE,"E36.0.6.10"),sQuery(id+"F4.wireOp",EDGE,"E36.0.6.15")])]})});
            var Q47;
            Q47=makeQuery(id+"F5.boolean.opBoolean","COPY",EDGE,{"derivedFrom":makeQuery(id+"F5.opExtrude","SWEPT_EDGE",EDGE,{"disambiguationData":[OSD([sQuery(id+"F4.wireOp",EDGE,"E36.0.5.10"),sQuery(id+"F4.wireOp",EDGE,"E36.0.5.15")])]})});
            var Q48;
            Q48=makeQuery(id+"F5.boolean.opBoolean","COPY",EDGE,{"derivedFrom":makeQuery(id+"F5.opExtrude","SWEPT_EDGE",EDGE,{"disambiguationData":[OSD([sQuery(id+"F4.wireOp",EDGE,"E36.0.4.10"),sQuery(id+"F4.wireOp",EDGE,"E36.0.4.15")])]})});
            var Q49;
            Q49=makeQuery(id+"F5.boolean.opBoolean","COPY",EDGE,{"derivedFrom":makeQuery(id+"F5.opExtrude","SWEPT_EDGE",EDGE,{"disambiguationData":[OSD([sQuery(id+"F4.wireOp",EDGE,"E36.0.3.10"),sQuery(id+"F4.wireOp",EDGE,"E36.0.3.15")])]})});
            var Q50;
            Q50=makeQuery(id+"F5.boolean.opBoolean","COPY",EDGE,{"derivedFrom":makeQuery(id+"F5.opExtrude","SWEPT_EDGE",EDGE,{"disambiguationData":[OSD([sQuery(id+"F4.wireOp",EDGE,"E36.0.3.2"),sQuery(id+"F4.wireOp",EDGE,"E36.0.3.11")])]})});
            var Q51;
            Q51=makeQuery(id+"F5.boolean.opBoolean","COPY",EDGE,{"derivedFrom":makeQuery(id+"F5.opExtrude","SWEPT_EDGE",EDGE,{"disambiguationData":[OSD([sQuery(id+"F4.wireOp",EDGE,"E36.0.3.5"),sQuery(id+"F4.wireOp",EDGE,"E36.0.3.9")])]})});
            var Q52;
            Q52=makeQuery(id+"F5.boolean.opBoolean","COPY",EDGE,{"derivedFrom":makeQuery(id+"F5.opExtrude","SWEPT_EDGE",EDGE,{"disambiguationData":[OSD([sQuery(id+"F4.wireOp",EDGE,"E36.0.4.2"),sQuery(id+"F4.wireOp",EDGE,"E36.0.4.11")])]})});
            var Q53;
            Q53=makeQuery(id+"F5.boolean.opBoolean","COPY",EDGE,{"derivedFrom":makeQuery(id+"F5.opExtrude","SWEPT_EDGE",EDGE,{"disambiguationData":[OSD([sQuery(id+"F4.wireOp",EDGE,"E36.0.4.5"),sQuery(id+"F4.wireOp",EDGE,"E36.0.4.9")])]})});
            var Q54;
            Q54=makeQuery(id+"F5.boolean.opBoolean","COPY",EDGE,{"derivedFrom":makeQuery(id+"F5.opExtrude","SWEPT_EDGE",EDGE,{"disambiguationData":[OSD([sQuery(id+"F4.wireOp",EDGE,"E36.0.5.5"),sQuery(id+"F4.wireOp",EDGE,"E36.0.5.9")])]})});
            var Q55;
            Q55=makeQuery(id+"F5.boolean.opBoolean","COPY",EDGE,{"derivedFrom":makeQuery(id+"F5.opExtrude","SWEPT_EDGE",EDGE,{"disambiguationData":[OSD([sQuery(id+"F4.wireOp",EDGE,"E36.0.5.2"),sQuery(id+"F4.wireOp",EDGE,"E36.0.5.11")])]})});
            var Q56;
            Q56=makeQuery(id+"F5.boolean.opBoolean","COPY",EDGE,{"derivedFrom":makeQuery(id+"F5.opExtrude","SWEPT_EDGE",EDGE,{"disambiguationData":[OSD([sQuery(id+"F4.wireOp",EDGE,"E36.0.6.2"),sQuery(id+"F4.wireOp",EDGE,"E36.0.6.11")])]})});
            var Q57;
            Q57=makeQuery(id+"F5.boolean.opBoolean","COPY",EDGE,{"derivedFrom":makeQuery(id+"F5.opExtrude","SWEPT_EDGE",EDGE,{"disambiguationData":[OSD([sQuery(id+"F4.wireOp",EDGE,"E36.0.6.5"),sQuery(id+"F4.wireOp",EDGE,"E36.0.6.9")])]})});
            var Q58;
            Q58=makeQuery(id+"F5.boolean.opBoolean","COPY",EDGE,{"derivedFrom":makeQuery(id+"F5.opExtrude","SWEPT_EDGE",EDGE,{"disambiguationData":[OSD([sQuery(id+"F4.wireOp",EDGE,"E26.top"),sQuery(id+"F4.wireOp",EDGE,"E26.right")])]})});
            var Q59;
            Q59=makeQuery(id+"F5.boolean.opBoolean","COPY",EDGE,{"derivedFrom":makeQuery(id+"F5.opExtrude","SWEPT_EDGE",EDGE,{"disambiguationData":[OSD([sQuery(id+"F4.wireOp",EDGE,"E29.MirrorCS"),sQuery(id+"F4.wireOp",EDGE,"E31.MirrorCS")])]})});
            var Q60;
            Q60=makeQuery(id+"F5.boolean.opBoolean","COPY",EDGE,{"derivedFrom":makeQuery(id+"F5.opExtrude","SWEPT_EDGE",EDGE,{"disambiguationData":[OSD([sQuery(id+"F4.wireOp",EDGE,"E28.MirrorCS"),sQuery(id+"F4.wireOp",EDGE,"E32.MirrorCS")])]})});
            var Q61;
            Q61=makeQuery(id+"F5.boolean.opBoolean","COPY",EDGE,{"derivedFrom":makeQuery(id+"F5.opExtrude","SWEPT_EDGE",EDGE,{"disambiguationData":[OSD([sQuery(id+"F4.wireOp",EDGE,"E36.0.1.5"),sQuery(id+"F4.wireOp",EDGE,"E36.0.1.7")])]})});
            var Q62;
            Q62=makeQuery(id+"F5.boolean.opBoolean","COPY",EDGE,{"derivedFrom":makeQuery(id+"F5.opExtrude","SWEPT_EDGE",EDGE,{"disambiguationData":[OSD([sQuery(id+"F4.wireOp",EDGE,"E36.0.1.6"),sQuery(id+"F4.wireOp",EDGE,"E36.0.1.11")])]})});
            var Q63;
            Q63=makeQuery(id+"F5.boolean.opBoolean","COPY",EDGE,{"derivedFrom":makeQuery(id+"F5.opExtrude","SWEPT_EDGE",EDGE,{"disambiguationData":[OSD([sQuery(id+"F4.wireOp",EDGE,"E36.0.1.4"),sQuery(id+"F4.wireOp",EDGE,"E36.0.1.15")])]})});
            var Q64;
            Q64=makeQuery(id+"F5.boolean.opBoolean","COPY",EDGE,{"derivedFrom":makeQuery(id+"F5.opExtrude","SWEPT_EDGE",EDGE,{"disambiguationData":[OSD([sQuery(id+"F4.wireOp",EDGE,"E36.0.1.1"),sQuery(id+"F4.wireOp",EDGE,"E36.0.1.8")])]})});
            var Q65;
            Q65=makeQuery(id+"F5.boolean.opBoolean","COPY",EDGE,{"derivedFrom":makeQuery(id+"F5.opExtrude","SWEPT_EDGE",EDGE,{"disambiguationData":[OSD([sQuery(id+"F4.wireOp",EDGE,"E36.0.2.1"),sQuery(id+"F4.wireOp",EDGE,"E36.0.2.8")])]})});
            var Q66;
            Q66=makeQuery(id+"F5.boolean.opBoolean","COPY",EDGE,{"derivedFrom":makeQuery(id+"F5.opExtrude","SWEPT_EDGE",EDGE,{"disambiguationData":[OSD([sQuery(id+"F4.wireOp",EDGE,"E36.0.2.4"),sQuery(id+"F4.wireOp",EDGE,"E36.0.2.15")])]})});
            var Q67;
            Q67=makeQuery(id+"F5.boolean.opBoolean","COPY",EDGE,{"derivedFrom":makeQuery(id+"F5.opExtrude","SWEPT_EDGE",EDGE,{"disambiguationData":[OSD([sQuery(id+"F4.wireOp",EDGE,"E36.0.2.6"),sQuery(id+"F4.wireOp",EDGE,"E36.0.2.11")])]})});
            var Q68;
            Q68=makeQuery(id+"F5.boolean.opBoolean","COPY",EDGE,{"derivedFrom":makeQuery(id+"F5.opExtrude","SWEPT_EDGE",EDGE,{"disambiguationData":[OSD([sQuery(id+"F4.wireOp",EDGE,"E36.0.2.5"),sQuery(id+"F4.wireOp",EDGE,"E36.0.2.7")])]})});
            var Q69;
            Q69=makeQuery(id+"F5.boolean.opBoolean","COPY",EDGE,{"derivedFrom":makeQuery(id+"F5.opExtrude","SWEPT_EDGE",EDGE,{"disambiguationData":[OSD([sQuery(id+"F4.wireOp",EDGE,"E36.0.3.5"),sQuery(id+"F4.wireOp",EDGE,"E36.0.3.7")])]})});
            var Q70;
            Q70=makeQuery(id+"F5.boolean.opBoolean","COPY",EDGE,{"derivedFrom":makeQuery(id+"F5.opExtrude","SWEPT_EDGE",EDGE,{"disambiguationData":[OSD([sQuery(id+"F4.wireOp",EDGE,"E36.0.3.6"),sQuery(id+"F4.wireOp",EDGE,"E36.0.3.11")])]})});
            var Q71;
            Q71=makeQuery(id+"F5.boolean.opBoolean","COPY",EDGE,{"derivedFrom":makeQuery(id+"F5.opExtrude","SWEPT_EDGE",EDGE,{"disambiguationData":[OSD([sQuery(id+"F4.wireOp",EDGE,"E36.0.3.4"),sQuery(id+"F4.wireOp",EDGE,"E36.0.3.15")])]})});
            var Q72;
            Q72=makeQuery(id+"F5.boolean.opBoolean","COPY",EDGE,{"derivedFrom":makeQuery(id+"F5.opExtrude","SWEPT_EDGE",EDGE,{"disambiguationData":[OSD([sQuery(id+"F4.wireOp",EDGE,"E36.0.3.1"),sQuery(id+"F4.wireOp",EDGE,"E36.0.3.8")])]})});
            var Q73;
            Q73=makeQuery(id+"F5.boolean.opBoolean","COPY",EDGE,{"derivedFrom":makeQuery(id+"F5.opExtrude","SWEPT_EDGE",EDGE,{"disambiguationData":[OSD([sQuery(id+"F4.wireOp",EDGE,"E36.0.4.1"),sQuery(id+"F4.wireOp",EDGE,"E36.0.4.8")])]})});
            var Q74;
            Q74=makeQuery(id+"F5.boolean.opBoolean","COPY",EDGE,{"derivedFrom":makeQuery(id+"F5.opExtrude","SWEPT_EDGE",EDGE,{"disambiguationData":[OSD([sQuery(id+"F4.wireOp",EDGE,"E36.0.4.4"),sQuery(id+"F4.wireOp",EDGE,"E36.0.4.15")])]})});
            var Q75;
            Q75=makeQuery(id+"F5.boolean.opBoolean","COPY",EDGE,{"derivedFrom":makeQuery(id+"F5.opExtrude","SWEPT_EDGE",EDGE,{"disambiguationData":[OSD([sQuery(id+"F4.wireOp",EDGE,"E36.0.4.6"),sQuery(id+"F4.wireOp",EDGE,"E36.0.4.11")])]})});
            var Q76;
            Q76=makeQuery(id+"F5.boolean.opBoolean","COPY",EDGE,{"derivedFrom":makeQuery(id+"F5.opExtrude","SWEPT_EDGE",EDGE,{"disambiguationData":[OSD([sQuery(id+"F4.wireOp",EDGE,"E36.0.4.5"),sQuery(id+"F4.wireOp",EDGE,"E36.0.4.7")])]})});
            var Q77;
            Q77=makeQuery(id+"F5.boolean.opBoolean","COPY",EDGE,{"derivedFrom":makeQuery(id+"F5.opExtrude","SWEPT_EDGE",EDGE,{"disambiguationData":[OSD([sQuery(id+"F4.wireOp",EDGE,"E36.0.5.5"),sQuery(id+"F4.wireOp",EDGE,"E36.0.5.7")])]})});
            var Q78;
            Q78=makeQuery(id+"F5.boolean.opBoolean","COPY",EDGE,{"derivedFrom":makeQuery(id+"F5.opExtrude","SWEPT_EDGE",EDGE,{"disambiguationData":[OSD([sQuery(id+"F4.wireOp",EDGE,"E36.0.5.6"),sQuery(id+"F4.wireOp",EDGE,"E36.0.5.11")])]})});
            var Q79;
            Q79=makeQuery(id+"F5.boolean.opBoolean","COPY",EDGE,{"derivedFrom":makeQuery(id+"F5.opExtrude","SWEPT_EDGE",EDGE,{"disambiguationData":[OSD([sQuery(id+"F4.wireOp",EDGE,"E36.0.5.4"),sQuery(id+"F4.wireOp",EDGE,"E36.0.5.15")])]})});
            var Q80;
            Q80=makeQuery(id+"F5.boolean.opBoolean","COPY",EDGE,{"derivedFrom":makeQuery(id+"F5.opExtrude","SWEPT_EDGE",EDGE,{"disambiguationData":[OSD([sQuery(id+"F4.wireOp",EDGE,"E36.0.5.1"),sQuery(id+"F4.wireOp",EDGE,"E36.0.5.8")])]})});
            var Q81;
            Q81=makeQuery(id+"F5.boolean.opBoolean","COPY",EDGE,{"derivedFrom":makeQuery(id+"F5.opExtrude","SWEPT_EDGE",EDGE,{"disambiguationData":[OSD([sQuery(id+"F4.wireOp",EDGE,"E36.0.6.1"),sQuery(id+"F4.wireOp",EDGE,"E36.0.6.8")])]})});
            var Q82;
            Q82=makeQuery(id+"F5.boolean.opBoolean","COPY",EDGE,{"derivedFrom":makeQuery(id+"F5.opExtrude","SWEPT_EDGE",EDGE,{"disambiguationData":[OSD([sQuery(id+"F4.wireOp",EDGE,"E36.0.6.4"),sQuery(id+"F4.wireOp",EDGE,"E36.0.6.15")])]})});
            var Q83;
            Q83=makeQuery(id+"F5.boolean.opBoolean","COPY",EDGE,{"derivedFrom":makeQuery(id+"F5.opExtrude","SWEPT_EDGE",EDGE,{"disambiguationData":[OSD([sQuery(id+"F4.wireOp",EDGE,"E36.0.6.6"),sQuery(id+"F4.wireOp",EDGE,"E36.0.6.11")])]})});
            var Q84;
            Q84=makeQuery(id+"F5.boolean.opBoolean","COPY",EDGE,{"derivedFrom":makeQuery(id+"F5.opExtrude","SWEPT_EDGE",EDGE,{"disambiguationData":[OSD([sQuery(id+"F4.wireOp",EDGE,"E36.0.6.5"),sQuery(id+"F4.wireOp",EDGE,"E36.0.6.7")])]})});
            var Q85;
            Q85=makeQuery(id+"F5.boolean.opBoolean","COPY",EDGE,{"derivedFrom":makeQuery(id+"F5.opExtrude","SWEPT_EDGE",EDGE,{"disambiguationData":[OSD([sQuery(id+"F4.wireOp",EDGE,"E26.bottom"),sQuery(id+"F4.wireOp",EDGE,"E26.right")])]})});
            var Q86;
            Q86=makeQuery(id+"F5.boolean.opBoolean","COPY",EDGE,{"derivedFrom":makeQuery(id+"F5.opExtrude","SWEPT_EDGE",EDGE,{"disambiguationData":[OSD([sQuery(id+"F4.wireOp",EDGE,"E31.MirrorCS"),sQuery(id+"F4.wireOp",EDGE,"E33.MirrorCS")])]})});
            var Q87;
            Q87=makeQuery(id+"F5.boolean.opBoolean","COPY",EDGE,{"derivedFrom":makeQuery(id+"F5.opExtrude","SWEPT_EDGE",EDGE,{"disambiguationData":[OSD([sQuery(id+"F4.wireOp",EDGE,"E30.MirrorCS"),sQuery(id+"F4.wireOp",EDGE,"E32.MirrorCS")])]})});
            var Q88;
            Q88=makeQuery(id+"F5.boolean.opBoolean","COPY",EDGE,{"derivedFrom":makeQuery(id+"F5.opExtrude","SWEPT_EDGE",EDGE,{"disambiguationData":[OSD([sQuery(id+"F4.wireOp",EDGE,"E36.0.1.8"),sQuery(id+"F4.wireOp",EDGE,"E36.0.1.14")])]})});
            var Q89;
            Q89=makeQuery(id+"F5.boolean.opBoolean","COPY",EDGE,{"derivedFrom":makeQuery(id+"F5.opExtrude","SWEPT_EDGE",EDGE,{"disambiguationData":[OSD([sQuery(id+"F4.wireOp",EDGE,"E36.0.1.0"),sQuery(id+"F4.wireOp",EDGE,"E36.0.1.4")])]})});
            var Q90;
            Q90=makeQuery(id+"F5.boolean.opBoolean","COPY",EDGE,{"derivedFrom":makeQuery(id+"F5.opExtrude","SWEPT_EDGE",EDGE,{"disambiguationData":[OSD([sQuery(id+"F4.wireOp",EDGE,"E36.0.1.6"),sQuery(id+"F4.wireOp",EDGE,"E36.0.1.12")])]})});
            var Q91;
            Q91=makeQuery(id+"F5.boolean.opBoolean","COPY",EDGE,{"derivedFrom":makeQuery(id+"F5.opExtrude","SWEPT_EDGE",EDGE,{"disambiguationData":[OSD([sQuery(id+"F4.wireOp",EDGE,"E36.0.1.3"),sQuery(id+"F4.wireOp",EDGE,"E36.0.1.7")])]})});
            var Q92;
            Q92=makeQuery(id+"F5.boolean.opBoolean","COPY",EDGE,{"derivedFrom":makeQuery(id+"F5.opExtrude","SWEPT_EDGE",EDGE,{"disambiguationData":[OSD([sQuery(id+"F4.wireOp",EDGE,"E36.0.2.8"),sQuery(id+"F4.wireOp",EDGE,"E36.0.2.14")])]})});
            var Q93;
            Q93=makeQuery(id+"F5.boolean.opBoolean","COPY",EDGE,{"derivedFrom":makeQuery(id+"F5.opExtrude","SWEPT_EDGE",EDGE,{"disambiguationData":[OSD([sQuery(id+"F4.wireOp",EDGE,"E36.0.2.0"),sQuery(id+"F4.wireOp",EDGE,"E36.0.2.4")])]})});
            var Q94;
            Q94=makeQuery(id+"F5.boolean.opBoolean","COPY",EDGE,{"derivedFrom":makeQuery(id+"F5.opExtrude","SWEPT_EDGE",EDGE,{"disambiguationData":[OSD([sQuery(id+"F4.wireOp",EDGE,"E36.0.2.6"),sQuery(id+"F4.wireOp",EDGE,"E36.0.2.12")])]})});
            var Q95;
            Q95=makeQuery(id+"F5.boolean.opBoolean","COPY",EDGE,{"derivedFrom":makeQuery(id+"F5.opExtrude","SWEPT_EDGE",EDGE,{"disambiguationData":[OSD([sQuery(id+"F4.wireOp",EDGE,"E36.0.2.3"),sQuery(id+"F4.wireOp",EDGE,"E36.0.2.7")])]})});
            var Q96;
            Q96=makeQuery(id+"F5.boolean.opBoolean","COPY",EDGE,{"derivedFrom":makeQuery(id+"F5.opExtrude","SWEPT_EDGE",EDGE,{"disambiguationData":[OSD([sQuery(id+"F4.wireOp",EDGE,"E36.0.3.8"),sQuery(id+"F4.wireOp",EDGE,"E36.0.3.14")])]})});
            var Q97;
            Q97=makeQuery(id+"F5.boolean.opBoolean","COPY",EDGE,{"derivedFrom":makeQuery(id+"F5.opExtrude","SWEPT_EDGE",EDGE,{"disambiguationData":[OSD([sQuery(id+"F4.wireOp",EDGE,"E36.0.3.0"),sQuery(id+"F4.wireOp",EDGE,"E36.0.3.4")])]})});
            var Q98;
            Q98=makeQuery(id+"F5.boolean.opBoolean","COPY",EDGE,{"derivedFrom":makeQuery(id+"F5.opExtrude","SWEPT_EDGE",EDGE,{"disambiguationData":[OSD([sQuery(id+"F4.wireOp",EDGE,"E36.0.3.6"),sQuery(id+"F4.wireOp",EDGE,"E36.0.3.12")])]})});
            var Q99;
            Q99=makeQuery(id+"F5.boolean.opBoolean","COPY",EDGE,{"derivedFrom":makeQuery(id+"F5.opExtrude","SWEPT_EDGE",EDGE,{"disambiguationData":[OSD([sQuery(id+"F4.wireOp",EDGE,"E36.0.3.3"),sQuery(id+"F4.wireOp",EDGE,"E36.0.3.7")])]})});
            var Q100;
            Q100=makeQuery(id+"F5.boolean.opBoolean","COPY",EDGE,{"derivedFrom":makeQuery(id+"F5.opExtrude","SWEPT_EDGE",EDGE,{"disambiguationData":[OSD([sQuery(id+"F4.wireOp",EDGE,"E36.0.4.8"),sQuery(id+"F4.wireOp",EDGE,"E36.0.4.14")])]})});
            var Q101;
            Q101=makeQuery(id+"F5.boolean.opBoolean","COPY",EDGE,{"derivedFrom":makeQuery(id+"F5.opExtrude","SWEPT_EDGE",EDGE,{"disambiguationData":[OSD([sQuery(id+"F4.wireOp",EDGE,"E36.0.4.0"),sQuery(id+"F4.wireOp",EDGE,"E36.0.4.4")])]})});
            var Q102;
            Q102=makeQuery(id+"F5.boolean.opBoolean","COPY",EDGE,{"derivedFrom":makeQuery(id+"F5.opExtrude","SWEPT_EDGE",EDGE,{"disambiguationData":[OSD([sQuery(id+"F4.wireOp",EDGE,"E36.0.4.6"),sQuery(id+"F4.wireOp",EDGE,"E36.0.4.12")])]})});
            var Q103;
            Q103=makeQuery(id+"F5.boolean.opBoolean","COPY",EDGE,{"derivedFrom":makeQuery(id+"F5.opExtrude","SWEPT_EDGE",EDGE,{"disambiguationData":[OSD([sQuery(id+"F4.wireOp",EDGE,"E36.0.4.3"),sQuery(id+"F4.wireOp",EDGE,"E36.0.4.7")])]})});
            var Q104;
            Q104=makeQuery(id+"F5.boolean.opBoolean","COPY",EDGE,{"derivedFrom":makeQuery(id+"F5.opExtrude","SWEPT_EDGE",EDGE,{"disambiguationData":[OSD([sQuery(id+"F4.wireOp",EDGE,"E36.0.5.8"),sQuery(id+"F4.wireOp",EDGE,"E36.0.5.14")])]})});
            var Q105;
            Q105=makeQuery(id+"F5.boolean.opBoolean","COPY",EDGE,{"derivedFrom":makeQuery(id+"F5.opExtrude","SWEPT_EDGE",EDGE,{"disambiguationData":[OSD([sQuery(id+"F4.wireOp",EDGE,"E36.0.5.0"),sQuery(id+"F4.wireOp",EDGE,"E36.0.5.4")])]})});
            var Q106;
            Q106=makeQuery(id+"F5.boolean.opBoolean","COPY",EDGE,{"derivedFrom":makeQuery(id+"F5.opExtrude","SWEPT_EDGE",EDGE,{"disambiguationData":[OSD([sQuery(id+"F4.wireOp",EDGE,"E36.0.5.6"),sQuery(id+"F4.wireOp",EDGE,"E36.0.5.12")])]})});
            var Q107;
            Q107=makeQuery(id+"F5.boolean.opBoolean","COPY",EDGE,{"derivedFrom":makeQuery(id+"F5.opExtrude","SWEPT_EDGE",EDGE,{"disambiguationData":[OSD([sQuery(id+"F4.wireOp",EDGE,"E36.0.5.3"),sQuery(id+"F4.wireOp",EDGE,"E36.0.5.7")])]})});
            var Q108;
            Q108=makeQuery(id+"F5.boolean.opBoolean","COPY",EDGE,{"derivedFrom":makeQuery(id+"F5.opExtrude","SWEPT_EDGE",EDGE,{"disambiguationData":[OSD([sQuery(id+"F4.wireOp",EDGE,"E36.0.6.8"),sQuery(id+"F4.wireOp",EDGE,"E36.0.6.14")])]})});
            var Q109;
            Q109=makeQuery(id+"F5.boolean.opBoolean","COPY",EDGE,{"derivedFrom":makeQuery(id+"F5.opExtrude","SWEPT_EDGE",EDGE,{"disambiguationData":[OSD([sQuery(id+"F4.wireOp",EDGE,"E36.0.6.0"),sQuery(id+"F4.wireOp",EDGE,"E36.0.6.4")])]})});
            var Q110;
            Q110=makeQuery(id+"F5.boolean.opBoolean","COPY",EDGE,{"derivedFrom":makeQuery(id+"F5.opExtrude","SWEPT_EDGE",EDGE,{"disambiguationData":[OSD([sQuery(id+"F4.wireOp",EDGE,"E36.0.6.6"),sQuery(id+"F4.wireOp",EDGE,"E36.0.6.12")])]})});
            var Q111;
            Q111=makeQuery(id+"F5.boolean.opBoolean","COPY",EDGE,{"derivedFrom":makeQuery(id+"F5.opExtrude","SWEPT_EDGE",EDGE,{"disambiguationData":[OSD([sQuery(id+"F4.wireOp",EDGE,"E36.0.6.3"),sQuery(id+"F4.wireOp",EDGE,"E36.0.6.7")])]})});
            fillet(context, id + "F6", {"entities" : qUnion([Q0, Q1, Q2, Q3, Q4, Q5, Q6, Q7, Q8, Q9, Q10, Q11, Q12, Q13, Q14, Q15, Q16, Q17, Q18, Q19, Q20, Q21, Q22, Q23, Q24, Q25, Q26, Q27, Q28, Q29, Q30, Q31, Q32, Q33, Q34, Q35, Q36, Q37, Q38, Q39, Q40, Q41, Q42, Q43, Q44, Q45, Q46, Q47, Q48, Q49, Q50, Q51, Q52, Q53, Q54, Q55, Q56, Q57, Q58, Q59, Q60, Q61, Q62, Q63, Q64, Q65, Q66, Q67, Q68, Q69, Q70, Q71, Q72, Q73, Q74, Q75, Q76, Q77, Q78, Q79, Q80, Q81, Q82, Q83, Q84, Q85, Q86, Q87, Q88, Q89, Q90, Q91, Q92, Q93, Q94, Q95, Q96, Q97, Q98, Q99, Q100, Q101, Q102, Q103, Q104, Q105, Q106, Q107, Q108, Q109, Q110, Q111]), "radius" : 1.59 * mm, "tangentPropagation" : true, "allowEdgeOverflow" : false});
        }
        {
            var Q0;
            Q0=makeQuery(id+"F1.opExtrude","CAP_FACE",FACE,{"disambiguationData":[OSD([sQuery(id+"F0.wireOp",EDGE,"E0.bottom"),sQuery(id+"F0.wireOp",EDGE,"E0.top"),sQuery(id+"F0.wireOp",EDGE,"E0.left"),sQuery(id+"F0.wireOp",EDGE,"E1"),sQuery(id+"F0.wireOp",EDGE,"E3.MirrorCS"),sQuery(id+"F0.wireOp",EDGE,"E4.MirrorC"),sQuery(id+"F0.wireOp",EDGE,"E7.MirrorC"),sQuery(id+"F0.wireOp",EDGE,"E12.MirrorC")])],"isStart":false});
            var sketch = newSketch(context, id + "F7", { "sketchPlane" : qUnion([Q0])});
            skLineSegment(sketch, "E38.bottom", {"start": v(54.15, -49.52) * mm, "end": v(-54.15, -49.52) * mm});
            skLineSegment(sketch, "E38.top", {"start": v(54.15, 30.48) * mm, "end": v(-54.15, 30.48) * mm});
            skLineSegment(sketch, "E38.left", {"start": v(54.15, -49.52) * mm, "end": v(54.15, 30.48) * mm});
            skLineSegment(sketch, "E38.right", {"start": v(-54.15, -49.52) * mm, "end": v(-54.15, 30.48) * mm});
            skPoint(sketch, "E38.middle", {"position": v(0, -9.52) * mm});
            skPoint(sketch, "E38.middle.positionSnap0", {"position": v(73.03, -9.52) * mm});
            skPoint(sketch, "E38.middle.positionSnap1", {"position": v(0, -57.15) * mm});
            skPoint(sketch, "E38.centerSnap0", {"position": v(73.03, -9.52) * mm});
            skPoint(sketch, "E38.centerSnap1", {"position": v(0, -57.15) * mm});
            skSolve(sketch);
        }
        {
            var Q0;
            Q0 = qSketchRegion(id + "F7", true);
            extrude(context, id + "F8", {"entities" : qUnion([Q0]), "operationType" : NewBodyOperationType.REMOVE, "oppositeDirection" : true, "depth" : 25 * mm, "offsetDistance" : 25 * mm});
        }
        {
            var Q0;
            Q0=makeQuery(id+"F1.opExtrude","CAP_FACE",FACE,{"disambiguationData":[OSD([sQuery(id+"F0.wireOp",EDGE,"E0.bottom"),sQuery(id+"F0.wireOp",EDGE,"E0.top"),sQuery(id+"F0.wireOp",EDGE,"E0.left"),sQuery(id+"F0.wireOp",EDGE,"E1"),sQuery(id+"F0.wireOp",EDGE,"E3.MirrorCS"),sQuery(id+"F0.wireOp",EDGE,"E4.MirrorC"),sQuery(id+"F0.wireOp",EDGE,"E7.MirrorC"),sQuery(id+"F0.wireOp",EDGE,"E12.MirrorC")])],"isStart":false});
            var sketch = newSketch(context, id + "F9", { "sketchPlane" : qUnion([Q0])});
            skLineSegment(sketch, "E39.bottom", {"start": v(-73.03, 38.1) * mm, "end": v(73.02, 38.1) * mm});
            skLineSegment(sketch, "E39.top", {"start": v(-73.03, 85.73) * mm, "end": v(73.02, 85.73) * mm});
            skLineSegment(sketch, "E39.left", {"start": v(-73.03, 38.1) * mm, "end": v(-73.03, 85.73) * mm});
            skLineSegment(sketch, "E39.right", {"start": v(73.02, 38.1) * mm, "end": v(73.02, 85.73) * mm});
            skCircle(sketch, "E40.MirrorC", {"center": v(68.26, 52.39) * mm, "radius": 3.24 * mm});
            skCircle(sketch, "E41.MirrorC", {"center": v(-68.26, 52.39) * mm, "radius": 3.24 * mm});
            skLineSegment(sketch, "E42", {"start": v(-73.03, 61.91) * mm, "end": v(-67.53, 61.91) * mm});
            skCircle(sketch, "E43.MirrorC", {"center": v(-68.26, 71.44) * mm, "radius": 3.24 * mm});
            skCircle(sketch, "E44.MirrorC", {"center": v(68.26, 71.44) * mm, "radius": 3.24 * mm});
            skSolve(sketch);
        }
        {
            var Q0;
            Q0 = qSketchRegion(id + "F9", true);
            extrude(context, id + "F10", {"entities" : qUnion([Q0]), "operationType" : NewBodyOperationType.ADD, "oppositeDirection" : true, "depth" : 3 * mm, "offsetDistance" : 25 * mm});
        }
    });
